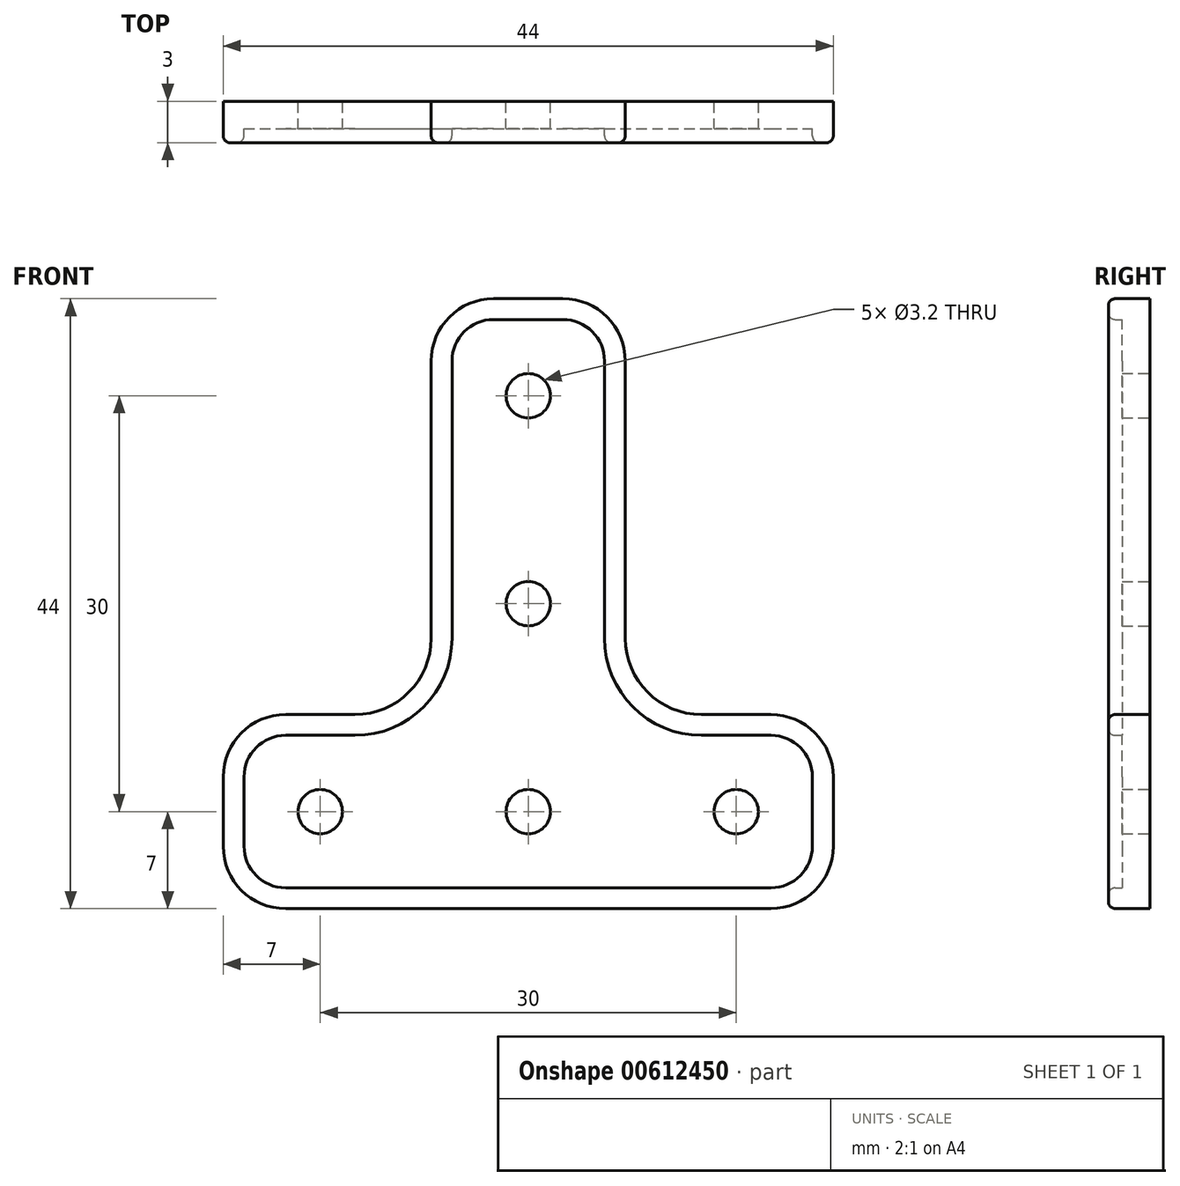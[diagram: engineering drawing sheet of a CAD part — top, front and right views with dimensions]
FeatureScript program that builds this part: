
annotation { "Feature Type Name" : "Feature", "Feature Type Description" : "" }
export const myFeature = defineFeature(function(context is Context, id is Id, definition is map)
    precondition{}
    {
        {
            var Q0;
            Q0=qCreatedBy(makeId("Front.planeOp"),FACE);
            var sketch = newSketch(context, id + "F0", { "sketchPlane" : qUnion([Q0])});
            skLineSegment(sketch, "E0", {"start": v(0, 44) * mm, "end": v(2.5, 44) * mm});
            skLineSegment(sketch, "E1", {"start": v(7, 39.5) * mm, "end": v(7, 19.5) * mm});
            skLineSegment(sketch, "E2", {"start": v(12.5, 14) * mm, "end": v(17.5, 14) * mm});
            skLineSegment(sketch, "E3", {"start": v(22, 9.5) * mm, "end": v(22, 4.5) * mm});
            skLineSegment(sketch, "E4", {"start": v(17.5, 0) * mm, "end": v(0, 0) * mm});
            skLineSegment(sketch, "E5", {"start": v(0, 0) * mm, "end": v(0, 44) * mm, "construction": true});
            skPoint(sketch, "E6.visualSharp", {"position": v(22, 0) * mm});
            skArc(sketch, "E6.filletArc", {"start": v(17.5, 0) * mm, "mid": v(20.68, 1.32) * mm, "end": v(22, 4.5) * mm});
            skPoint(sketch, "E7.visualSharp", {"position": v(22, 14) * mm});
            skArc(sketch, "E7.filletArc", {"start": v(22, 9.5) * mm, "mid": v(20.68, 12.68) * mm, "end": v(17.5, 14) * mm});
            skPoint(sketch, "E8.visualSharp", {"position": v(7, 14) * mm});
            skArc(sketch, "E8.filletArc", {"start": v(7, 19.5) * mm, "mid": v(8.61, 15.61) * mm, "end": v(12.5, 14) * mm});
            skPoint(sketch, "E9.visualSharp", {"position": v(7, 44) * mm});
            skArc(sketch, "E9.filletArc", {"start": v(7, 39.5) * mm, "mid": v(5.68, 42.68) * mm, "end": v(2.5, 44) * mm});
            skLineSegment(sketch, "E10.MirrorCS", {"start": v(-17.5, 0) * mm, "end": v(0, 0) * mm});
            skArc(sketch, "E11.MirrorCS", {"start": v(-17.5, 0) * mm, "mid": v(-20.68, 1.32) * mm, "end": v(-22, 4.5) * mm});
            skLineSegment(sketch, "E12.MirrorCS", {"start": v(-22, 9.5) * mm, "end": v(-22, 4.5) * mm});
            skArc(sketch, "E13.MirrorCS", {"start": v(-22, 9.5) * mm, "mid": v(-20.68, 12.68) * mm, "end": v(-17.5, 14) * mm});
            skLineSegment(sketch, "E14.MirrorCS", {"start": v(-12.5, 14) * mm, "end": v(-17.5, 14) * mm});
            skArc(sketch, "E15.MirrorCS", {"start": v(-7, 19.5) * mm, "mid": v(-8.61, 15.61) * mm, "end": v(-12.5, 14) * mm});
            skLineSegment(sketch, "E16.MirrorCS", {"start": v(-7, 39.5) * mm, "end": v(-7, 19.5) * mm});
            skArc(sketch, "E17.MirrorCS", {"start": v(-7, 39.5) * mm, "mid": v(-5.68, 42.68) * mm, "end": v(-2.5, 44) * mm});
            skLineSegment(sketch, "E18.MirrorCS", {"start": v(0, 44) * mm, "end": v(-2.5, 44) * mm});
            skCircle(sketch, "E19", {"center": v(0, 7) * mm, "radius": 1.6 * mm});
            skCircle(sketch, "E20", {"center": v(15, 7) * mm, "radius": 1.6 * mm});
            skCircle(sketch, "E21", {"center": v(-15, 7) * mm, "radius": 1.6 * mm});
            skCircle(sketch, "E22", {"center": v(0, 22) * mm, "radius": 1.6 * mm});
            skCircle(sketch, "E23", {"center": v(0, 37) * mm, "radius": 1.6 * mm});
            skSolve(sketch);
        }
        {
            var Q0;
            Q0=makeQuery(id+"F0.imprint","IMPRINT",FACE,{"disambiguationData":[TD([[makeQuery(id+"F0.imprint","IMPRINT",EDGE,{"derivedFrom":sQuery(id+"F0.wireOp",EDGE,"E0")}),-1.0]])]});
            extrude(context, id + "F1", {"entities" : qUnion([Q0]), "depth" : 2 * mm, "offsetDistance" : 25 * mm});
        }
        {
            var Q0;
            Q0=makeQuery(id+"F1.opExtrude","CAP_FACE",FACE,{"disambiguationData":[OSD([sQuery(id+"F0.wireOp",EDGE,"E0"),sQuery(id+"F0.wireOp",EDGE,"E1"),sQuery(id+"F0.wireOp",EDGE,"E2"),sQuery(id+"F0.wireOp",EDGE,"E3"),sQuery(id+"F0.wireOp",EDGE,"E4"),sQuery(id+"F0.wireOp",EDGE,"E6.filletArc"),sQuery(id+"F0.wireOp",EDGE,"E7.filletArc"),sQuery(id+"F0.wireOp",EDGE,"E8.filletArc"),sQuery(id+"F0.wireOp",EDGE,"E9.filletArc"),sQuery(id+"F0.wireOp",EDGE,"E10.MirrorCS"),sQuery(id+"F0.wireOp",EDGE,"E11.MirrorCS"),sQuery(id+"F0.wireOp",EDGE,"E12.MirrorCS"),sQuery(id+"F0.wireOp",EDGE,"E13.MirrorCS"),sQuery(id+"F0.wireOp",EDGE,"E14.MirrorCS"),sQuery(id+"F0.wireOp",EDGE,"E15.MirrorCS"),sQuery(id+"F0.wireOp",EDGE,"E16.MirrorCS"),sQuery(id+"F0.wireOp",EDGE,"E17.MirrorCS"),sQuery(id+"F0.wireOp",EDGE,"E18.MirrorCS"),sQuery(id+"F0.wireOp",EDGE,"E19"),sQuery(id+"F0.wireOp",EDGE,"E20"),sQuery(id+"F0.wireOp",EDGE,"E21"),sQuery(id+"F0.wireOp",EDGE,"E22"),sQuery(id+"F0.wireOp",EDGE,"E23")])],"isStart":false});
            var sketch = newSketch(context, id + "F2", { "sketchPlane" : qUnion([Q0])});
            skLineSegment(sketch, "E24.0", {"start": v(-5.5, 39.5) * mm, "end": v(-5.5, 19.5) * mm});
            skArc(sketch, "E24.1", {"start": v(-5.5, 39.5) * mm, "mid": v(-4.62, 41.62) * mm, "end": v(-2.5, 42.5) * mm});
            skLineSegment(sketch, "E24.2", {"start": v(-2.5, 42.5) * mm, "end": v(2.5, 42.5) * mm});
            skArc(sketch, "E24.3", {"start": v(5.5, 39.5) * mm, "mid": v(4.62, 41.62) * mm, "end": v(2.5, 42.5) * mm});
            skLineSegment(sketch, "E24.4", {"start": v(5.5, 39.5) * mm, "end": v(5.5, 19.5) * mm});
            skArc(sketch, "E24.5", {"start": v(-17.5, 1.5) * mm, "mid": v(-19.62, 2.38) * mm, "end": v(-20.5, 4.5) * mm});
            skLineSegment(sketch, "E24.6", {"start": v(-20.5, 9.5) * mm, "end": v(-20.5, 4.5) * mm});
            skArc(sketch, "E24.7", {"start": v(-20.5, 9.5) * mm, "mid": v(-19.62, 11.62) * mm, "end": v(-17.5, 12.5) * mm});
            skLineSegment(sketch, "E24.8", {"start": v(-12.5, 12.5) * mm, "end": v(-17.5, 12.5) * mm});
            skLineSegment(sketch, "E24.9", {"start": v(-17.5, 1.5) * mm, "end": v(17.5, 1.5) * mm});
            skArc(sketch, "E24.10", {"start": v(17.5, 1.5) * mm, "mid": v(19.62, 2.38) * mm, "end": v(20.5, 4.5) * mm});
            skLineSegment(sketch, "E24.11", {"start": v(20.5, 9.5) * mm, "end": v(20.5, 4.5) * mm});
            skArc(sketch, "E24.12", {"start": v(20.5, 9.5) * mm, "mid": v(19.62, 11.62) * mm, "end": v(17.5, 12.5) * mm});
            skLineSegment(sketch, "E24.13", {"start": v(12.5, 12.5) * mm, "end": v(17.5, 12.5) * mm});
            skArc(sketch, "E24.14", {"start": v(-5.5, 19.5) * mm, "mid": v(-7.55, 14.55) * mm, "end": v(-12.5, 12.5) * mm});
            skArc(sketch, "E24.15", {"start": v(5.5, 19.5) * mm, "mid": v(7.55, 14.55) * mm, "end": v(12.5, 12.5) * mm});
            skSolve(sketch);
        }
        {
            var Q0;
            Q0=makeQuery(id+"F2.imprint","IMPRINT",FACE,{"disambiguationData":[TD([[makeQuery(id+"F2.imprint","IMPRINT",EDGE,{"derivedFrom":sQuery(id+"F2.wireOp",EDGE,"E24.0")}),-1.0]])]});
            extrude(context, id + "F3", {"entities" : qUnion([Q0]), "operationType" : NewBodyOperationType.ADD, "depth" : 1 * mm, "offsetDistance" : 25 * mm});
        }
        {
            var Q0;
            Q0=makeQuery(id+"F3.opExtrude","CAP_EDGE",EDGE,{"disambiguationData":[OSD([sQuery(id+"F0.wireOp",EDGE,"E16.MirrorCS")])],"isStart":false});
            var Q1;
            Q1=makeQuery(id+"F3.opExtrude","CAP_EDGE",EDGE,{"disambiguationData":[OSD([sQuery(id+"F2.wireOp",EDGE,"E24.0")])],"isStart":false});
            fillet(context, id + "F4", {"entities" : qUnion([Q0, Q1]), "radius" : 0.5 * mm, "tangentPropagation" : true, "allowEdgeOverflow" : false});
        }
    });
